annotation { "Feature Type Name" : "Feature", "Feature Type Description" : "" }
export const myFeature = defineFeature(function(context is Context, id is Id, definition is map)
    precondition{}
    {
        {
            var Q0;
            Q0=qCreatedBy(makeId("Front.planeOp"),FACE);
            var sketch = newSketch(context, id + "F0", { "sketchPlane" : qUnion([Q0])});
            skLineSegment(sketch, "E0.top", {"start": v(-50, -15) * mm, "end": v(50, -15) * mm});
            skLineSegment(sketch, "E0.left", {"start": v(-50, 15) * mm, "end": v(-50, -15) * mm});
            skLineSegment(sketch, "E0.right", {"start": v(50, 15) * mm, "end": v(50, -15) * mm});
            skPoint(sketch, "E1", {"position": v(0, 15) * mm});
            skPoint(sketch, "E2", {"position": v(-50, 0) * mm});
            skPoint(sketch, "E3", {"position": v(-19.95, 15) * mm});
            skPoint(sketch, "E4", {"position": v(19.95, 15) * mm});
            skArc(sketch, "E5", {"start": v(19.95, 15) * mm, "mid": v(0, 34.95) * mm, "end": v(-19.95, 15) * mm});
            skLineSegment(sketch, "E6", {"start": v(-50, 15) * mm, "end": v(-19.95, 15) * mm});
            skLineSegment(sketch, "E7", {"start": v(19.95, 15) * mm, "end": v(50, 15) * mm});
            skCircle(sketch, "E8", {"center": v(0, 25.93) * mm, "radius": 2.5 * mm});
            skText(sketch, "E9", { "text": "Sebastian Ewald", "fontName": "OpenSans-Bold.ttf"});
            const initialGuessF0  = {"E9": [-0.045, -0.00902, 1, 0, 0.00802]};
            skSetInitialGuess(sketch, initialGuessF0);
            skSolve(sketch);
        }
        {
            var Q0;
            Q0=makeQuery(id+"F0.imprint","IMPRINT",FACE,{"disambiguationData":[TD([[makeQuery(id+"F0.imprint","IMPRINT",EDGE,{"derivedFrom":sQuery(id+"F0.wireOp",EDGE,"E0.top")}),1.0]])]});
            extrude(context, id + "F1", {"entities" : qUnion([Q0]), "oppositeDirection" : true, "depth" : 10 * mm});
        }
    });